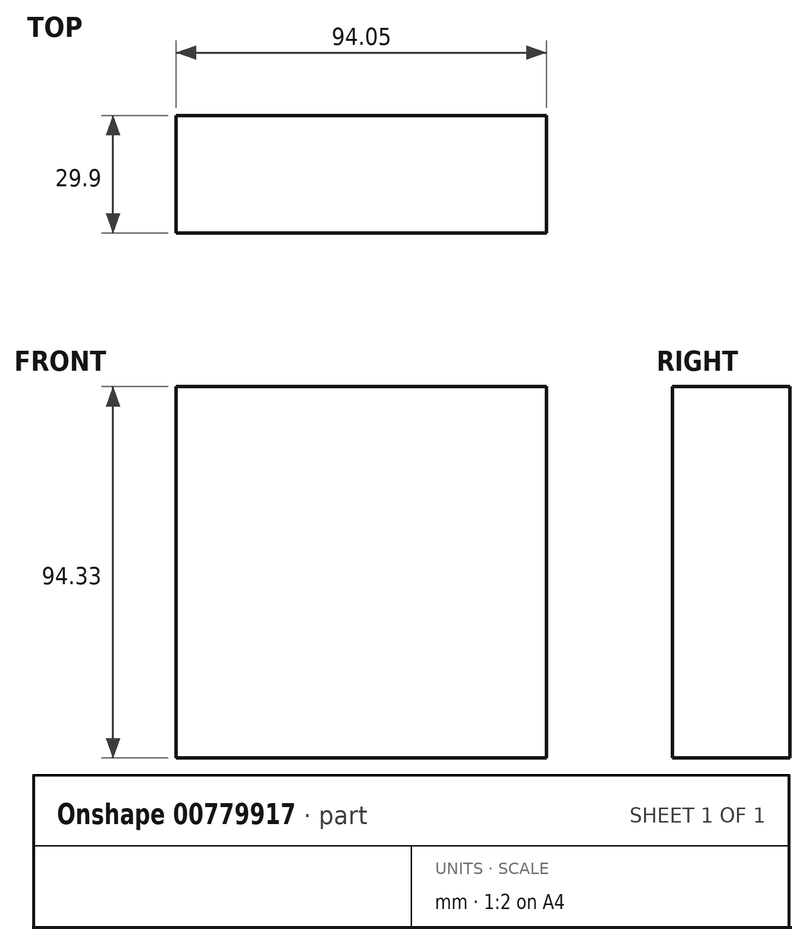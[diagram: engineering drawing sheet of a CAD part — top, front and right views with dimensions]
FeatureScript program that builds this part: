
annotation { "Feature Type Name" : "Feature", "Feature Type Description" : "" }
export const myFeature = defineFeature(function(context is Context, id is Id, definition is map)
    precondition{}
    {
        {
            var Q0;
            Q0=qCreatedBy(makeId("Front.planeOp"),FACE);
            var sketch = newSketch(context, id + "F0", { "sketchPlane" : qUnion([Q0])});
            skLineSegment(sketch, "E0.bottom", {"start": v(-50, 43.2) * mm, "end": v(44.05, 43.2) * mm});
            skLineSegment(sketch, "E0.top", {"start": v(-50, -51.13) * mm, "end": v(44.05, -51.13) * mm});
            skLineSegment(sketch, "E0.left", {"start": v(-50, 43.2) * mm, "end": v(-50, -51.13) * mm});
            skLineSegment(sketch, "E0.right", {"start": v(44.05, 43.2) * mm, "end": v(44.05, -51.13) * mm});
            skSolve(sketch);
        }
        {
            var Q0;
            Q0 = qSketchRegion(id + "F0", true);
            extrude(context, id + "F1", {"entities" : qUnion([Q0]), "endBound" : BoundingType.SYMMETRIC, "depth" : 29.9 * mm, "offsetDistance" : 25 * mm});
        }
    });
